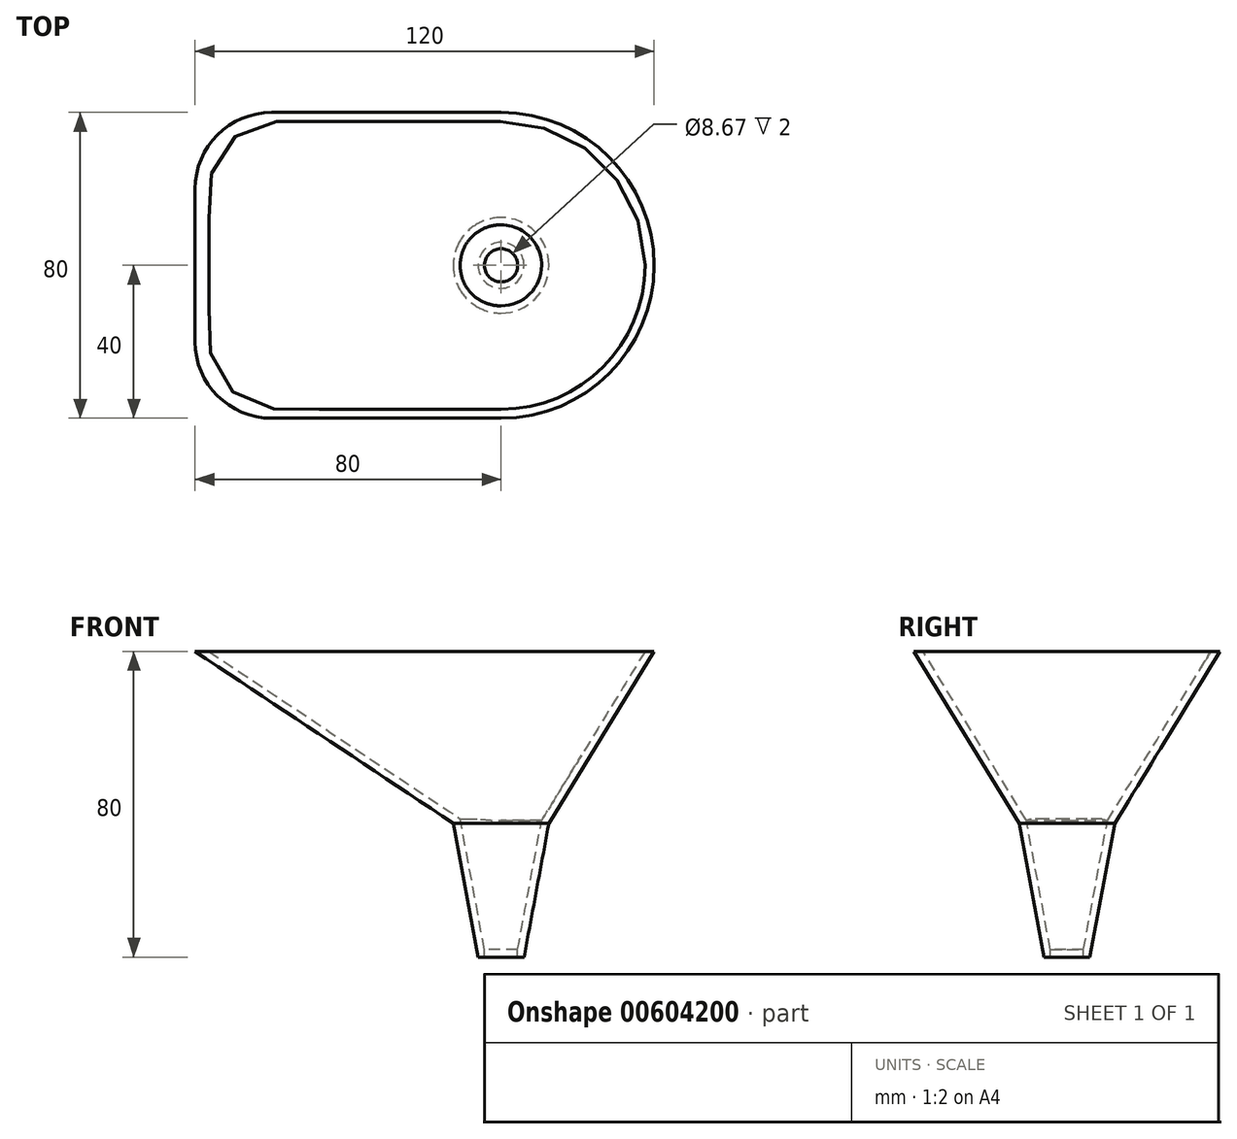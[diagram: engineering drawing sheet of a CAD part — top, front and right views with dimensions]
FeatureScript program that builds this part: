
annotation { "Feature Type Name" : "Feature", "Feature Type Description" : "" }
export const myFeature = defineFeature(function(context is Context, id is Id, definition is map)
    precondition{}
    {
        {
            var Q0;
            Q0=qCreatedBy(makeId("Top.planeOp"),FACE);
            var sketch = newSketch(context, id + "F0", { "sketchPlane" : qUnion([Q0])});
            skCircle(sketch, "E0", {"center": v(0, 0) * mm, "radius": 12.5 * mm});
            skSolve(sketch);
        }
        {
            var Q0;
            Q0=qCreatedBy(makeId("Top.planeOp"),FACE);
            cPlane(context, id + "F1", {"entities" : qUnion([Q0]), "cplaneType" : CPlaneType.OFFSET, "offset" : 35 * mm, "oppositeDirection" : true, "width" : 150 * mm, "height" : 150 * mm});
        }
        {
            var Q0;
            Q0=qCreatedBy(id+"F1.planeOp",FACE);
            var sketch = newSketch(context, id + "F2", { "sketchPlane" : qUnion([Q0])});
            skCircle(sketch, "E1", {"center": v(0, 0) * mm, "radius": 6 * mm});
            skSolve(sketch);
        }
        {
            var Q0;
            Q0=makeQuery(id+"F0.imprint","IMPRINT",FACE,{"disambiguationData":[TD([[makeQuery(id+"F0.imprint","IMPRINT",EDGE,{"derivedFrom":sQuery(id+"F0.wireOp",EDGE,"E0")}),1.0]])]});
            var Q1;
            Q1=makeQuery(id+"F2.imprint","IMPRINT",FACE,{"disambiguationData":[TD([[makeQuery(id+"F2.imprint","IMPRINT",EDGE,{"derivedFrom":sQuery(id+"F2.wireOp",EDGE,"E1")}),1.0]])]});
            loft(context, id + "F3", {"sheetProfilesArray" : [{ "sheetProfileEntities" : qUnion([Q0]) }, { "sheetProfileEntities" : qUnion([Q1]) }]});
        }
        {
            var Q0;
            Q0=qCreatedBy(makeId("Top.planeOp"),FACE);
            cPlane(context, id + "F4", {"entities" : qUnion([Q0]), "cplaneType" : CPlaneType.OFFSET, "offset" : 45 * mm, "width" : 150 * mm, "height" : 150 * mm});
        }
        {
            var Q0;
            Q0=qCreatedBy(id+"F4.planeOp",FACE);
            var sketch = newSketch(context, id + "F5", { "sketchPlane" : qUnion([Q0])});
            skLineSegment(sketch, "E2", {"start": v(0, -40) * mm, "end": v(-60, -40) * mm});
            skLineSegment(sketch, "E3", {"start": v(-80, -20) * mm, "end": v(-80, 20) * mm});
            skLineSegment(sketch, "E4", {"start": v(-60, 40) * mm, "end": v(0, 40) * mm});
            skArc(sketch, "E5", {"start": v(0, 40) * mm, "mid": v(40, 0) * mm, "end": v(0, -40) * mm});
            skPoint(sketch, "E6.visualSharp", {"position": v(-80, -40) * mm});
            skArc(sketch, "E6.filletArc", {"start": v(-80, -20) * mm, "mid": v(-74.14, -34.14) * mm, "end": v(-60, -40) * mm});
            skPoint(sketch, "E7.visualSharp", {"position": v(-80, 40) * mm});
            skArc(sketch, "E7.filletArc", {"start": v(-60, 40) * mm, "mid": v(-74.14, 34.14) * mm, "end": v(-80, 20) * mm});
            skSolve(sketch);
        }
        {
            var Q0;
            Q0=qCreatedBy(makeId("Right.planeOp"),FACE);
            var sketch = newSketch(context, id + "F6", { "sketchPlane" : qUnion([Q0])});
            skLineSegment(sketch, "E8", {"start": v(40, 45) * mm, "end": v(12.5, 0) * mm});
            skLineSegment(sketch, "E9", {"start": v(-40, 45) * mm, "end": v(-12.5, 0) * mm});
            skSolve(sketch);
        }
        {
            var Q0;
            Q0=qCreatedBy(makeId("Front.planeOp"),FACE);
            var sketch = newSketch(context, id + "F7", { "sketchPlane" : qUnion([Q0])});
            skLineSegment(sketch, "E10", {"start": v(40, 45) * mm, "end": v(12.5, 0) * mm});
            skLineSegment(sketch, "E11", {"start": v(-80, 45) * mm, "end": v(-12.5, 0) * mm});
            skSolve(sketch);
        }
        {
            var Q0;
            Q0=makeQuery(id+"F5.imprint","IMPRINT",FACE,{"disambiguationData":[TD([[makeQuery(id+"F5.imprint","IMPRINT",EDGE,{"derivedFrom":sQuery(id+"F5.wireOp",EDGE,"E2")}),-1.0]])]});
            var Q1;
            Q1=makeQuery(id+"F3.opLoft","CAP_FACE",FACE,{"disambiguationData":[OSD([makeQuery(id+"F0.imprint","IMPRINT",FACE,{"disambiguationData":[TD([[makeQuery(id+"F0.imprint","IMPRINT",EDGE,{"derivedFrom":sQuery(id+"F0.wireOp",EDGE,"E0")}),1.0]])]})])],"isStart":true});
            var Q2;
            Q2=sQuery(id+"F7.wireOp",EDGE,"E10");
            var Q3;
            Q3=sQuery(id+"F6.wireOp",EDGE,"E8");
            var Q4;
            Q4=sQuery(id+"F6.wireOp",EDGE,"E9");
            var Q5;
            Q5=sQuery(id+"F7.wireOp",EDGE,"E11");
            loft(context, id + "F8", {"operationType" : NewBodyOperationType.ADD, "addGuides" : true, "sheetProfilesArray" : [{ "sheetProfileEntities" : qUnion([Q0]) }, { "sheetProfileEntities" : qUnion([Q1]) }], "guidesArray" : [{ "guideEntities" : qUnion([Q2]), "guideDerivativeType" : LoftGuideDerivativeType.DEFAULT, "guideDerivativeMagnitude" : 1 }, { "guideEntities" : qUnion([Q3]), "guideDerivativeType" : LoftGuideDerivativeType.DEFAULT, "guideDerivativeMagnitude" : 1 }, { "guideEntities" : qUnion([Q4]), "guideDerivativeType" : LoftGuideDerivativeType.DEFAULT, "guideDerivativeMagnitude" : 1 }, { "guideEntities" : qUnion([Q5]), "guideDerivativeType" : LoftGuideDerivativeType.DEFAULT, "guideDerivativeMagnitude" : 1 }]});
        }
        {
            var Q0;
            Q0=makeQuery(id+"F8.opLoft","CAP_FACE",FACE,{"disambiguationData":[OSD([makeQuery(id+"F5.imprint","IMPRINT",FACE,{"disambiguationData":[TD([[makeQuery(id+"F5.imprint","IMPRINT",EDGE,{"derivedFrom":sQuery(id+"F5.wireOp",EDGE,"E2")}),-1.0]])]})])],"isStart":true});
            shell(context, id + "F9", {"entities" : qUnion([Q0]), "thickness" : 2 * mm});
        }
        {
            var Q0;
            Q0=makeQuery(id+"F9.opShell","OFFSET_FACE",FACE,{"disambiguationData":[OSD([makeQuery(id+"F2.imprint","IMPRINT",FACE,{"disambiguationData":[TD([[makeQuery(id+"F2.imprint","IMPRINT",EDGE,{"derivedFrom":sQuery(id+"F2.wireOp",EDGE,"E1")}),1.0]])]})])]});
            extrude(context, id + "F10", {"entities" : qUnion([Q0]), "operationType" : NewBodyOperationType.REMOVE, "endBound" : BoundingType.THROUGH_ALL, "oppositeDirection" : true, "depth" : 25 * mm, "offsetDistance" : 25 * mm});
        }
    });
